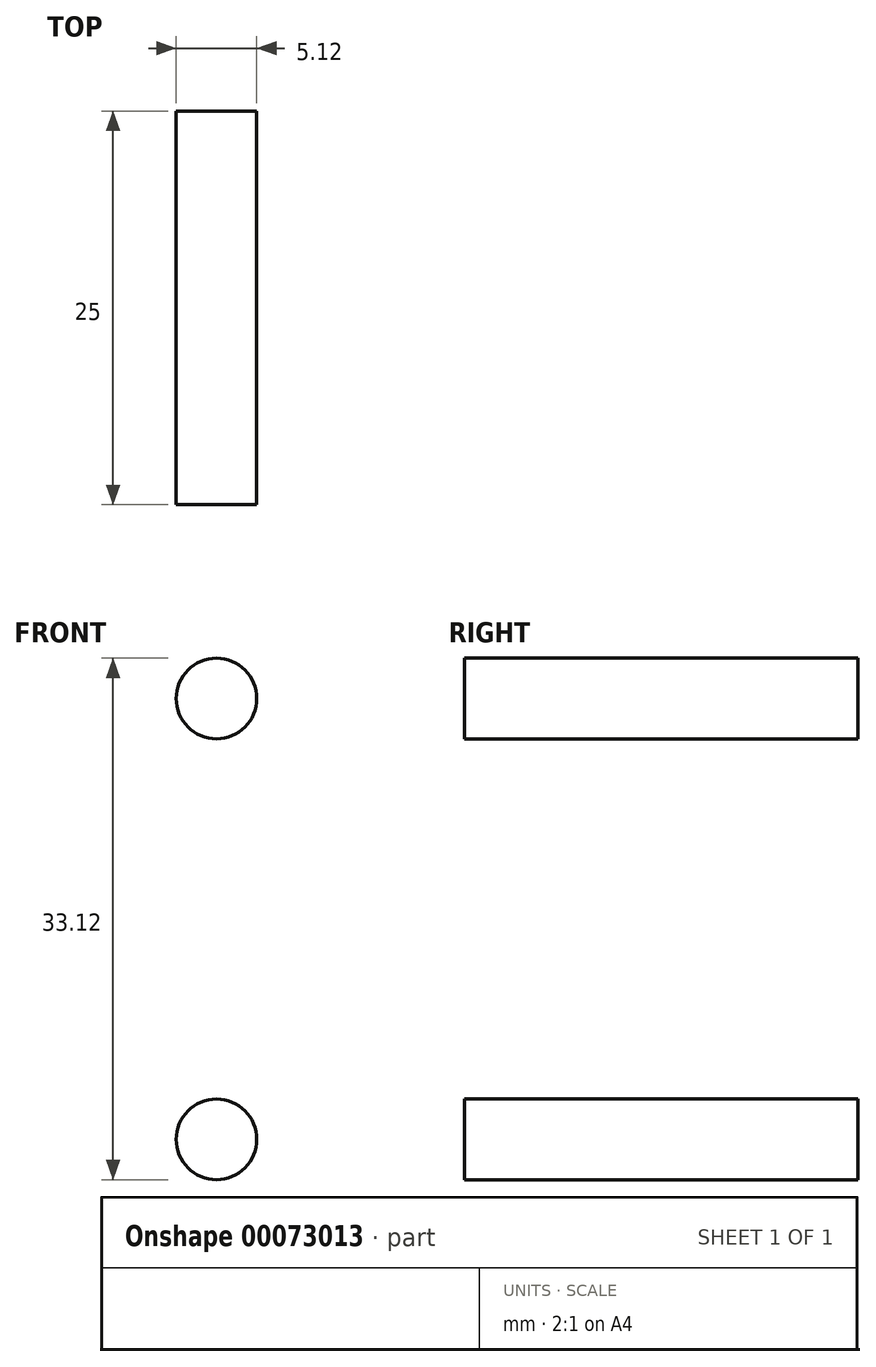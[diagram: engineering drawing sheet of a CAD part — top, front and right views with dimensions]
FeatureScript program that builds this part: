
annotation { "Feature Type Name" : "Feature", "Feature Type Description" : "" }
export const myFeature = defineFeature(function(context is Context, id is Id, definition is map)
    precondition{}
    {
        {
            var Q0;
            Q0=qCreatedBy(makeId("Front.planeOp"),FACE);
            var sketch = newSketch(context, id + "F0", { "sketchPlane" : qUnion([Q0])});
            skCircle(sketch, "E0", {"center": v(0, 0) * mm, "radius": 2.56 * mm});
            skArc(sketch, "E1", {"start": v(-1.68, -4.42) * mm, "mid": v(-2.88, -4.66) * mm, "end": v(-3.9, -5.34) * mm});
            skLineSegment(sketch, "E2", {"start": v(-1.68, -4.42) * mm, "end": v(1.68, -4.42) * mm});
            skArc(sketch, "E3", {"start": v(3.9, -5.34) * mm, "mid": v(2.88, -4.66) * mm, "end": v(1.68, -4.43) * mm});
            skLineSegment(sketch, "E4", {"start": v(3.9, -5.34) * mm, "end": v(7.07, -8.5) * mm});
            skArc(sketch, "E5", {"start": v(6.32, -10.32) * mm, "mid": v(7.3, -9.67) * mm, "end": v(7.07, -8.5) * mm});
            skLineSegment(sketch, "E6", {"start": v(6.32, -10.33) * mm, "end": v(4.22, -10.33) * mm});
            skArc(sketch, "E7", {"start": v(4.22, -10.32) * mm, "mid": v(3.49, -10.63) * mm, "end": v(3.19, -11.36) * mm});
            skLineSegment(sketch, "E8", {"start": v(3.19, -11.36) * mm, "end": v(3.19, -11.47) * mm});
            skArc(sketch, "E9", {"start": v(3.19, -11.47) * mm, "mid": v(3.49, -12.2) * mm, "end": v(4.22, -12.5) * mm});
            skLineSegment(sketch, "E10", {"start": v(4.22, -12.5) * mm, "end": v(5.23, -12.5) * mm});
            skArc(sketch, "E11", {"start": v(6.23, -12.5) * mm, "mid": v(5.73, -12) * mm, "end": v(5.23, -12.5) * mm});
            skLineSegment(sketch, "E12", {"start": v(6.23, -12.5) * mm, "end": v(9.4, -12.5) * mm});
            skArc(sketch, "E13", {"start": v(10.4, -12.5) * mm, "mid": v(9.9, -12) * mm, "end": v(9.4, -12.5) * mm});
            skArc(sketch, "E14", {"start": v(10.4, -12.5) * mm, "mid": v(11.9, -11.9) * mm, "end": v(12.5, -10.4) * mm});
            skArc(sketch, "E15", {"start": v(12.5, -9.4) * mm, "mid": v(12, -9.9) * mm, "end": v(12.5, -10.4) * mm});
            skLineSegment(sketch, "E16", {"start": v(12.5, -9.4) * mm, "end": v(12.5, -6.23) * mm});
            skArc(sketch, "E17", {"start": v(12.5, -5.23) * mm, "mid": v(12, -5.73) * mm, "end": v(12.5, -6.23) * mm});
            skLineSegment(sketch, "E18", {"start": v(12.5, -5.23) * mm, "end": v(12.5, -4.22) * mm});
            skArc(sketch, "E19", {"start": v(12.5, -4.22) * mm, "mid": v(12.2, -3.49) * mm, "end": v(11.47, -3.19) * mm});
            skLineSegment(sketch, "E20", {"start": v(11.47, -3.19) * mm, "end": v(11.36, -3.19) * mm});
            skArc(sketch, "E21", {"start": v(11.36, -3.19) * mm, "mid": v(10.63, -3.49) * mm, "end": v(10.32, -4.22) * mm});
            skLineSegment(sketch, "E22", {"start": v(10.33, -4.22) * mm, "end": v(10.33, -6.3) * mm});
            skArc(sketch, "E23", {"start": v(8.6, -7.02) * mm, "mid": v(9.7, -7.24) * mm, "end": v(10.33, -6.3) * mm});
            skLineSegment(sketch, "E24", {"start": v(8.6, -7.02) * mm, "end": v(5.36, -3.78) * mm});
            skArc(sketch, "E25", {"start": v(4.44, -1.57) * mm, "mid": v(4.68, -2.77) * mm, "end": v(5.36, -3.78) * mm});
            skLineSegment(sketch, "E26", {"start": v(4.44, -1.57) * mm, "end": v(4.44, 1.57) * mm});
            skArc(sketch, "E27", {"start": v(5.36, 3.78) * mm, "mid": v(4.68, 2.77) * mm, "end": v(4.44, 1.57) * mm});
            skLineSegment(sketch, "E28", {"start": v(5.36, 3.78) * mm, "end": v(8.6, 7.02) * mm});
            skArc(sketch, "E29", {"start": v(10.33, 6.3) * mm, "mid": v(9.7, 7.24) * mm, "end": v(8.6, 7.02) * mm});
            skLineSegment(sketch, "E30", {"start": v(10.33, 6.3) * mm, "end": v(10.33, 4.22) * mm});
            skArc(sketch, "E31", {"start": v(10.32, 4.22) * mm, "mid": v(10.63, 3.49) * mm, "end": v(11.36, 3.19) * mm});
            skLineSegment(sketch, "E32", {"start": v(11.36, 3.19) * mm, "end": v(11.47, 3.19) * mm});
            skArc(sketch, "E33", {"start": v(11.47, 3.19) * mm, "mid": v(12.2, 3.49) * mm, "end": v(12.5, 4.22) * mm});
            skLineSegment(sketch, "E34", {"start": v(12.5, 4.22) * mm, "end": v(12.5, 5.23) * mm});
            skArc(sketch, "E35", {"start": v(12.5, 6.23) * mm, "mid": v(12, 5.73) * mm, "end": v(12.5, 5.23) * mm});
            skLineSegment(sketch, "E36", {"start": v(12.5, 6.23) * mm, "end": v(12.5, 9.4) * mm});
            skArc(sketch, "E37", {"start": v(12.5, 10.4) * mm, "mid": v(12, 9.9) * mm, "end": v(12.5, 9.4) * mm});
            skArc(sketch, "E38", {"start": v(12.5, 10.4) * mm, "mid": v(11.9, 11.9) * mm, "end": v(10.4, 12.5) * mm});
            skArc(sketch, "E39", {"start": v(9.4, 12.5) * mm, "mid": v(9.9, 12) * mm, "end": v(10.4, 12.5) * mm});
            skLineSegment(sketch, "E40", {"start": v(9.4, 12.5) * mm, "end": v(6.23, 12.5) * mm});
            skArc(sketch, "E41", {"start": v(5.23, 12.5) * mm, "mid": v(5.73, 12) * mm, "end": v(6.23, 12.5) * mm});
            skLineSegment(sketch, "E42", {"start": v(5.23, 12.5) * mm, "end": v(4.22, 12.5) * mm});
            skArc(sketch, "E43", {"start": v(4.22, 12.5) * mm, "mid": v(3.49, 12.2) * mm, "end": v(3.19, 11.47) * mm});
            skLineSegment(sketch, "E44", {"start": v(3.19, 11.47) * mm, "end": v(3.19, 11.36) * mm});
            skArc(sketch, "E45", {"start": v(3.19, 11.36) * mm, "mid": v(3.49, 10.63) * mm, "end": v(4.22, 10.32) * mm});
            skLineSegment(sketch, "E46", {"start": v(4.22, 10.33) * mm, "end": v(6.37, 10.33) * mm});
            skArc(sketch, "E47", {"start": v(7.1, 8.59) * mm, "mid": v(7.32, 9.7) * mm, "end": v(6.37, 10.32) * mm});
            skLineSegment(sketch, "E48", {"start": v(7.1, 8.59) * mm, "end": v(3.84, 5.34) * mm});
            skArc(sketch, "E49", {"start": v(1.63, 4.42) * mm, "mid": v(2.82, 4.66) * mm, "end": v(3.84, 5.34) * mm});
            skLineSegment(sketch, "E50", {"start": v(1.63, 4.42) * mm, "end": v(-1.63, 4.42) * mm});
            skArc(sketch, "E51", {"start": v(-3.84, 5.34) * mm, "mid": v(-2.82, 4.66) * mm, "end": v(-1.63, 4.42) * mm});
            skLineSegment(sketch, "E52", {"start": v(-3.84, 5.34) * mm, "end": v(-7.1, 8.59) * mm});
            skArc(sketch, "E53", {"start": v(-6.37, 10.32) * mm, "mid": v(-7.32, 9.7) * mm, "end": v(-7.1, 8.59) * mm});
            skLineSegment(sketch, "E54", {"start": v(-6.37, 10.33) * mm, "end": v(-4.22, 10.33) * mm});
            skArc(sketch, "E55", {"start": v(-4.22, 10.32) * mm, "mid": v(-3.49, 10.63) * mm, "end": v(-3.19, 11.36) * mm});
            skLineSegment(sketch, "E56", {"start": v(-3.19, 11.36) * mm, "end": v(-3.19, 11.47) * mm});
            skArc(sketch, "E57", {"start": v(-3.19, 11.47) * mm, "mid": v(-3.49, 12.2) * mm, "end": v(-4.22, 12.5) * mm});
            skLineSegment(sketch, "E58", {"start": v(-4.22, 12.5) * mm, "end": v(-5.23, 12.5) * mm});
            skArc(sketch, "E59", {"start": v(-6.23, 12.5) * mm, "mid": v(-5.73, 12) * mm, "end": v(-5.23, 12.5) * mm});
            skLineSegment(sketch, "E60", {"start": v(-6.23, 12.5) * mm, "end": v(-9.4, 12.5) * mm});
            skArc(sketch, "E61", {"start": v(-10.4, 12.5) * mm, "mid": v(-9.9, 12) * mm, "end": v(-9.4, 12.5) * mm});
            skArc(sketch, "E62", {"start": v(-10.4, 12.5) * mm, "mid": v(-11.9, 11.9) * mm, "end": v(-12.5, 10.4) * mm});
            skArc(sketch, "E63", {"start": v(-12.5, 9.4) * mm, "mid": v(-12, 9.9) * mm, "end": v(-12.5, 10.4) * mm});
            skLineSegment(sketch, "E64", {"start": v(-12.5, 9.4) * mm, "end": v(-12.5, 6.23) * mm});
            skArc(sketch, "E65", {"start": v(-12.5, 5.23) * mm, "mid": v(-12, 5.73) * mm, "end": v(-12.5, 6.23) * mm});
            skLineSegment(sketch, "E66", {"start": v(-12.5, 5.23) * mm, "end": v(-12.5, 4.22) * mm});
            skArc(sketch, "E67", {"start": v(-12.5, 4.22) * mm, "mid": v(-12.2, 3.49) * mm, "end": v(-11.47, 3.19) * mm});
            skLineSegment(sketch, "E68", {"start": v(-11.47, 3.19) * mm, "end": v(-11.36, 3.19) * mm});
            skArc(sketch, "E69", {"start": v(-11.36, 3.19) * mm, "mid": v(-10.63, 3.49) * mm, "end": v(-10.32, 4.22) * mm});
            skLineSegment(sketch, "E70", {"start": v(-10.33, 4.22) * mm, "end": v(-10.33, 6.3) * mm});
            skArc(sketch, "E71", {"start": v(-8.6, 7.02) * mm, "mid": v(-9.7, 7.24) * mm, "end": v(-10.33, 6.3) * mm});
            skLineSegment(sketch, "E72", {"start": v(-8.6, 7.02) * mm, "end": v(-5.36, 3.78) * mm});
            skArc(sketch, "E73", {"start": v(-4.44, 1.57) * mm, "mid": v(-4.68, 2.77) * mm, "end": v(-5.36, 3.78) * mm});
            skLineSegment(sketch, "E74", {"start": v(-4.44, 1.57) * mm, "end": v(-4.44, -1.57) * mm});
            skArc(sketch, "E75", {"start": v(-5.36, -3.78) * mm, "mid": v(-4.68, -2.77) * mm, "end": v(-4.44, -1.57) * mm});
            skLineSegment(sketch, "E76", {"start": v(-5.36, -3.78) * mm, "end": v(-8.6, -7.02) * mm});
            skArc(sketch, "E77", {"start": v(-10.33, -6.3) * mm, "mid": v(-9.7, -7.24) * mm, "end": v(-8.6, -7.02) * mm});
            skLineSegment(sketch, "E78", {"start": v(-10.33, -6.3) * mm, "end": v(-10.33, -4.22) * mm});
            skArc(sketch, "E79", {"start": v(-10.32, -4.22) * mm, "mid": v(-10.63, -3.49) * mm, "end": v(-11.36, -3.19) * mm});
            skLineSegment(sketch, "E80", {"start": v(-11.36, -3.19) * mm, "end": v(-11.47, -3.19) * mm});
            skArc(sketch, "E81", {"start": v(-11.47, -3.19) * mm, "mid": v(-12.2, -3.49) * mm, "end": v(-12.5, -4.22) * mm});
            skLineSegment(sketch, "E82", {"start": v(-12.5, -4.22) * mm, "end": v(-12.5, -5.23) * mm});
            skArc(sketch, "E83", {"start": v(-12.5, -6.23) * mm, "mid": v(-12, -5.73) * mm, "end": v(-12.5, -5.23) * mm});
            skLineSegment(sketch, "E84", {"start": v(-12.5, -6.23) * mm, "end": v(-12.5, -9.4) * mm});
            skArc(sketch, "E85", {"start": v(-12.5, -10.4) * mm, "mid": v(-12, -9.9) * mm, "end": v(-12.5, -9.4) * mm});
            skArc(sketch, "E86", {"start": v(-12.5, -10.4) * mm, "mid": v(-11.9, -11.9) * mm, "end": v(-10.4, -12.5) * mm});
            skArc(sketch, "E87", {"start": v(-9.4, -12.5) * mm, "mid": v(-9.9, -12) * mm, "end": v(-10.4, -12.5) * mm});
            skLineSegment(sketch, "E88", {"start": v(-9.4, -12.5) * mm, "end": v(-6.23, -12.5) * mm});
            skArc(sketch, "E89", {"start": v(-5.23, -12.5) * mm, "mid": v(-5.73, -12) * mm, "end": v(-6.23, -12.5) * mm});
            skLineSegment(sketch, "E90", {"start": v(-5.23, -12.5) * mm, "end": v(-4.22, -12.5) * mm});
            skArc(sketch, "E91", {"start": v(-4.22, -12.5) * mm, "mid": v(-3.49, -12.2) * mm, "end": v(-3.19, -11.47) * mm});
            skLineSegment(sketch, "E92", {"start": v(-3.19, -11.47) * mm, "end": v(-3.19, -11.36) * mm});
            skArc(sketch, "E93", {"start": v(-3.19, -11.36) * mm, "mid": v(-3.49, -10.63) * mm, "end": v(-4.22, -10.32) * mm});
            skLineSegment(sketch, "E94", {"start": v(-4.22, -10.33) * mm, "end": v(-6.32, -10.33) * mm});
            skArc(sketch, "E95", {"start": v(-7.07, -8.5) * mm, "mid": v(-7.3, -9.67) * mm, "end": v(-6.32, -10.32) * mm});
            skLineSegment(sketch, "E96", {"start": v(-7.07, -8.5) * mm, "end": v(-3.9, -5.34) * mm});
            skSolve(sketch);
        }
        {
            assignVariable(context, id + "F1", {"name" : "DistanceBetweenBars", "anyValue" : 3});
        }
        {
            var Q0;
            Q0=makeQuery(id+"F0.imprint","IMPRINT",FACE,{"disambiguationData":[TD([[makeQuery(id+"F0.imprint","IMPRINT",EDGE,{"derivedFrom":sQuery(id+"F0.wireOp",EDGE,"E0")}),1.0]])]});
            extrude(context, id + "F2", {"entities" : qUnion([Q0]), "endBound" : BoundingType.SYMMETRIC, "depth" : 25 * mm});
        }
        {
            var Q0;
            Q0=makeQuery(id+"F2.opExtrude","SWEPT_BODY",BODY,{"disambiguationData":[OSD([sQuery(id+"F0.wireOp",EDGE,"E0"),sQuery(id+"F0.wireOp",EDGE,"E1"),sQuery(id+"F0.wireOp",EDGE,"E2"),sQuery(id+"F0.wireOp",EDGE,"E3"),sQuery(id+"F0.wireOp",EDGE,"E4"),sQuery(id+"F0.wireOp",EDGE,"E5"),sQuery(id+"F0.wireOp",EDGE,"E6"),sQuery(id+"F0.wireOp",EDGE,"E7"),sQuery(id+"F0.wireOp",EDGE,"E8"),sQuery(id+"F0.wireOp",EDGE,"E9"),sQuery(id+"F0.wireOp",EDGE,"E10"),sQuery(id+"F0.wireOp",EDGE,"E11"),sQuery(id+"F0.wireOp",EDGE,"E12"),sQuery(id+"F0.wireOp",EDGE,"E13"),sQuery(id+"F0.wireOp",EDGE,"E14"),sQuery(id+"F0.wireOp",EDGE,"E15"),sQuery(id+"F0.wireOp",EDGE,"E16"),sQuery(id+"F0.wireOp",EDGE,"E17"),sQuery(id+"F0.wireOp",EDGE,"E18"),sQuery(id+"F0.wireOp",EDGE,"E19"),sQuery(id+"F0.wireOp",EDGE,"E20"),sQuery(id+"F0.wireOp",EDGE,"E21"),sQuery(id+"F0.wireOp",EDGE,"E22"),sQuery(id+"F0.wireOp",EDGE,"E23"),sQuery(id+"F0.wireOp",EDGE,"E24"),sQuery(id+"F0.wireOp",EDGE,"E25"),sQuery(id+"F0.wireOp",EDGE,"E26"),sQuery(id+"F0.wireOp",EDGE,"E27"),sQuery(id+"F0.wireOp",EDGE,"E28"),sQuery(id+"F0.wireOp",EDGE,"E29"),sQuery(id+"F0.wireOp",EDGE,"E30"),sQuery(id+"F0.wireOp",EDGE,"E31"),sQuery(id+"F0.wireOp",EDGE,"E32"),sQuery(id+"F0.wireOp",EDGE,"E33"),sQuery(id+"F0.wireOp",EDGE,"E34"),sQuery(id+"F0.wireOp",EDGE,"E35"),sQuery(id+"F0.wireOp",EDGE,"E36"),sQuery(id+"F0.wireOp",EDGE,"E37"),sQuery(id+"F0.wireOp",EDGE,"E38"),sQuery(id+"F0.wireOp",EDGE,"E39"),sQuery(id+"F0.wireOp",EDGE,"E40"),sQuery(id+"F0.wireOp",EDGE,"E41"),sQuery(id+"F0.wireOp",EDGE,"E42"),sQuery(id+"F0.wireOp",EDGE,"E43"),sQuery(id+"F0.wireOp",EDGE,"E44"),sQuery(id+"F0.wireOp",EDGE,"E45"),sQuery(id+"F0.wireOp",EDGE,"E46"),sQuery(id+"F0.wireOp",EDGE,"E47"),sQuery(id+"F0.wireOp",EDGE,"E48"),sQuery(id+"F0.wireOp",EDGE,"E49"),sQuery(id+"F0.wireOp",EDGE,"E50"),sQuery(id+"F0.wireOp",EDGE,"E51"),sQuery(id+"F0.wireOp",EDGE,"E52"),sQuery(id+"F0.wireOp",EDGE,"E53"),sQuery(id+"F0.wireOp",EDGE,"E54"),sQuery(id+"F0.wireOp",EDGE,"E55"),sQuery(id+"F0.wireOp",EDGE,"E56"),sQuery(id+"F0.wireOp",EDGE,"E57"),sQuery(id+"F0.wireOp",EDGE,"E58"),sQuery(id+"F0.wireOp",EDGE,"E59"),sQuery(id+"F0.wireOp",EDGE,"E60"),sQuery(id+"F0.wireOp",EDGE,"E61"),sQuery(id+"F0.wireOp",EDGE,"E62"),sQuery(id+"F0.wireOp",EDGE,"E63"),sQuery(id+"F0.wireOp",EDGE,"E64"),sQuery(id+"F0.wireOp",EDGE,"E65"),sQuery(id+"F0.wireOp",EDGE,"E66"),sQuery(id+"F0.wireOp",EDGE,"E67"),sQuery(id+"F0.wireOp",EDGE,"E68"),sQuery(id+"F0.wireOp",EDGE,"E69"),sQuery(id+"F0.wireOp",EDGE,"E70"),sQuery(id+"F0.wireOp",EDGE,"E71"),sQuery(id+"F0.wireOp",EDGE,"E72"),sQuery(id+"F0.wireOp",EDGE,"E73"),sQuery(id+"F0.wireOp",EDGE,"E74"),sQuery(id+"F0.wireOp",EDGE,"E75"),sQuery(id+"F0.wireOp",EDGE,"E76"),sQuery(id+"F0.wireOp",EDGE,"E77"),sQuery(id+"F0.wireOp",EDGE,"E78"),sQuery(id+"F0.wireOp",EDGE,"E79"),sQuery(id+"F0.wireOp",EDGE,"E80"),sQuery(id+"F0.wireOp",EDGE,"E81"),sQuery(id+"F0.wireOp",EDGE,"E82"),sQuery(id+"F0.wireOp",EDGE,"E83"),sQuery(id+"F0.wireOp",EDGE,"E84"),sQuery(id+"F0.wireOp",EDGE,"E85"),sQuery(id+"F0.wireOp",EDGE,"E86"),sQuery(id+"F0.wireOp",EDGE,"E87"),sQuery(id+"F0.wireOp",EDGE,"E88"),sQuery(id+"F0.wireOp",EDGE,"E89"),sQuery(id+"F0.wireOp",EDGE,"E90"),sQuery(id+"F0.wireOp",EDGE,"E91"),sQuery(id+"F0.wireOp",EDGE,"E92"),sQuery(id+"F0.wireOp",EDGE,"E93"),sQuery(id+"F0.wireOp",EDGE,"E94"),sQuery(id+"F0.wireOp",EDGE,"E95"),sQuery(id+"F0.wireOp",EDGE,"E96")])]});
            var Q1;
            Q1=qCreatedBy(makeId("Top.planeOp"),FACE);
            transform(context, id + "F3", {"entities" : qUnion([Q0]), "transformType" : TransformType.TRANSLATION_DISTANCE, "transformDirection" : qUnion([Q1]), "distance" : ((25 + getVariable(context, 'DistanceBetweenBars')) / 2) * mm, "makeCopy" : false});
        }
        {
            var Q0;
            Q0=makeQuery(id+"F2.opExtrude","SWEPT_BODY",BODY,{"disambiguationData":[OSD([sQuery(id+"F0.wireOp",EDGE,"E0"),sQuery(id+"F0.wireOp",EDGE,"E1"),sQuery(id+"F0.wireOp",EDGE,"E2"),sQuery(id+"F0.wireOp",EDGE,"E3"),sQuery(id+"F0.wireOp",EDGE,"E4"),sQuery(id+"F0.wireOp",EDGE,"E5"),sQuery(id+"F0.wireOp",EDGE,"E6"),sQuery(id+"F0.wireOp",EDGE,"E7"),sQuery(id+"F0.wireOp",EDGE,"E8"),sQuery(id+"F0.wireOp",EDGE,"E9"),sQuery(id+"F0.wireOp",EDGE,"E10"),sQuery(id+"F0.wireOp",EDGE,"E11"),sQuery(id+"F0.wireOp",EDGE,"E12"),sQuery(id+"F0.wireOp",EDGE,"E13"),sQuery(id+"F0.wireOp",EDGE,"E14"),sQuery(id+"F0.wireOp",EDGE,"E15"),sQuery(id+"F0.wireOp",EDGE,"E16"),sQuery(id+"F0.wireOp",EDGE,"E17"),sQuery(id+"F0.wireOp",EDGE,"E18"),sQuery(id+"F0.wireOp",EDGE,"E19"),sQuery(id+"F0.wireOp",EDGE,"E20"),sQuery(id+"F0.wireOp",EDGE,"E21"),sQuery(id+"F0.wireOp",EDGE,"E22"),sQuery(id+"F0.wireOp",EDGE,"E23"),sQuery(id+"F0.wireOp",EDGE,"E24"),sQuery(id+"F0.wireOp",EDGE,"E25"),sQuery(id+"F0.wireOp",EDGE,"E26"),sQuery(id+"F0.wireOp",EDGE,"E27"),sQuery(id+"F0.wireOp",EDGE,"E28"),sQuery(id+"F0.wireOp",EDGE,"E29"),sQuery(id+"F0.wireOp",EDGE,"E30"),sQuery(id+"F0.wireOp",EDGE,"E31"),sQuery(id+"F0.wireOp",EDGE,"E32"),sQuery(id+"F0.wireOp",EDGE,"E33"),sQuery(id+"F0.wireOp",EDGE,"E34"),sQuery(id+"F0.wireOp",EDGE,"E35"),sQuery(id+"F0.wireOp",EDGE,"E36"),sQuery(id+"F0.wireOp",EDGE,"E37"),sQuery(id+"F0.wireOp",EDGE,"E38"),sQuery(id+"F0.wireOp",EDGE,"E39"),sQuery(id+"F0.wireOp",EDGE,"E40"),sQuery(id+"F0.wireOp",EDGE,"E41"),sQuery(id+"F0.wireOp",EDGE,"E42"),sQuery(id+"F0.wireOp",EDGE,"E43"),sQuery(id+"F0.wireOp",EDGE,"E44"),sQuery(id+"F0.wireOp",EDGE,"E45"),sQuery(id+"F0.wireOp",EDGE,"E46"),sQuery(id+"F0.wireOp",EDGE,"E47"),sQuery(id+"F0.wireOp",EDGE,"E48"),sQuery(id+"F0.wireOp",EDGE,"E49"),sQuery(id+"F0.wireOp",EDGE,"E50"),sQuery(id+"F0.wireOp",EDGE,"E51"),sQuery(id+"F0.wireOp",EDGE,"E52"),sQuery(id+"F0.wireOp",EDGE,"E53"),sQuery(id+"F0.wireOp",EDGE,"E54"),sQuery(id+"F0.wireOp",EDGE,"E55"),sQuery(id+"F0.wireOp",EDGE,"E56"),sQuery(id+"F0.wireOp",EDGE,"E57"),sQuery(id+"F0.wireOp",EDGE,"E58"),sQuery(id+"F0.wireOp",EDGE,"E59"),sQuery(id+"F0.wireOp",EDGE,"E60"),sQuery(id+"F0.wireOp",EDGE,"E61"),sQuery(id+"F0.wireOp",EDGE,"E62"),sQuery(id+"F0.wireOp",EDGE,"E63"),sQuery(id+"F0.wireOp",EDGE,"E64"),sQuery(id+"F0.wireOp",EDGE,"E65"),sQuery(id+"F0.wireOp",EDGE,"E66"),sQuery(id+"F0.wireOp",EDGE,"E67"),sQuery(id+"F0.wireOp",EDGE,"E68"),sQuery(id+"F0.wireOp",EDGE,"E69"),sQuery(id+"F0.wireOp",EDGE,"E70"),sQuery(id+"F0.wireOp",EDGE,"E71"),sQuery(id+"F0.wireOp",EDGE,"E72"),sQuery(id+"F0.wireOp",EDGE,"E73"),sQuery(id+"F0.wireOp",EDGE,"E74"),sQuery(id+"F0.wireOp",EDGE,"E75"),sQuery(id+"F0.wireOp",EDGE,"E76"),sQuery(id+"F0.wireOp",EDGE,"E77"),sQuery(id+"F0.wireOp",EDGE,"E78"),sQuery(id+"F0.wireOp",EDGE,"E79"),sQuery(id+"F0.wireOp",EDGE,"E80"),sQuery(id+"F0.wireOp",EDGE,"E81"),sQuery(id+"F0.wireOp",EDGE,"E82"),sQuery(id+"F0.wireOp",EDGE,"E83"),sQuery(id+"F0.wireOp",EDGE,"E84"),sQuery(id+"F0.wireOp",EDGE,"E85"),sQuery(id+"F0.wireOp",EDGE,"E86"),sQuery(id+"F0.wireOp",EDGE,"E87"),sQuery(id+"F0.wireOp",EDGE,"E88"),sQuery(id+"F0.wireOp",EDGE,"E89"),sQuery(id+"F0.wireOp",EDGE,"E90"),sQuery(id+"F0.wireOp",EDGE,"E91"),sQuery(id+"F0.wireOp",EDGE,"E92"),sQuery(id+"F0.wireOp",EDGE,"E93"),sQuery(id+"F0.wireOp",EDGE,"E94"),sQuery(id+"F0.wireOp",EDGE,"E95"),sQuery(id+"F0.wireOp",EDGE,"E96")])]});
            var Q1;
            Q1=qCreatedBy(makeId("Top.planeOp"),FACE);
            mirror(context, id + "F4", {"entities" : qUnion([Q0]), "mirrorPlane" : qUnion([Q1])});
        }
    });
